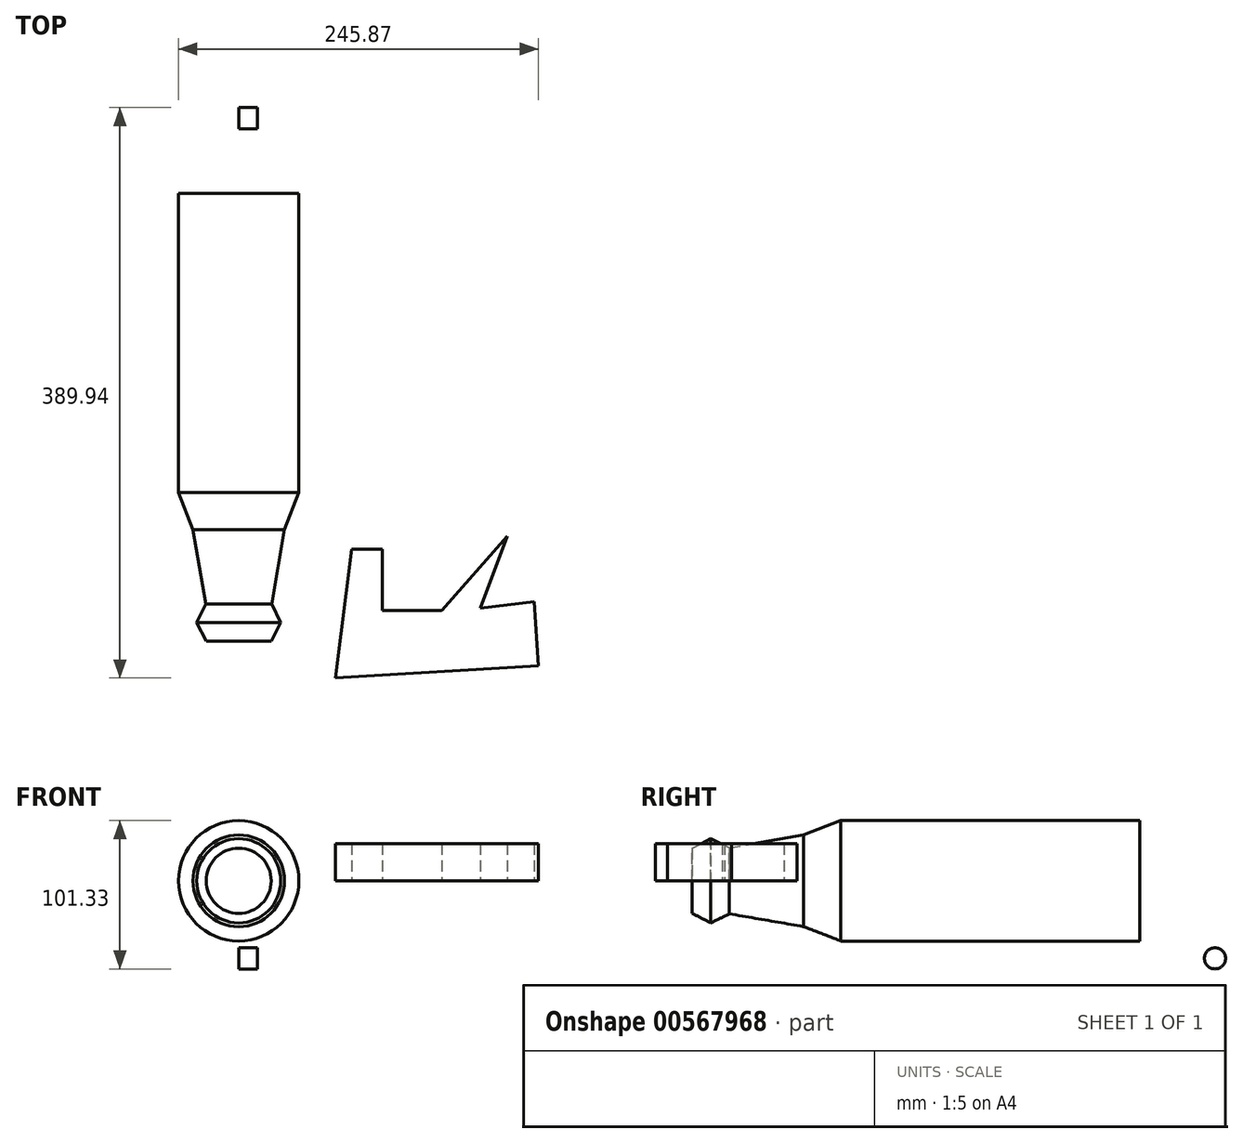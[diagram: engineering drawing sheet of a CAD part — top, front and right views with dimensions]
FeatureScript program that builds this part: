
annotation { "Feature Type Name" : "Feature", "Feature Type Description" : "" }
export const myFeature = defineFeature(function(context is Context, id is Id, definition is map)
    precondition{}
    {
        {
            var Q0;
            Q0=qCreatedBy(makeId("Front.planeOp"),FACE);
            var sketch = newSketch(context, id + "F0", { "sketchPlane" : qUnion([Q0])});
            skCircle(sketch, "E0", {"center": v(0, 0) * mm, "radius": 41.12 * mm});
            skSolve(sketch);
        }
        {
            var Q0;
            Q0 = qSketchRegion(id + "F0", true);
            extrude(context, id + "F1", {"entities" : qUnion([Q0]), "depth" : 204.47 * mm, "offsetDistance" : 25.4 * mm});
        }
        {
            var Q0;
            Q0=makeQuery(id+"F1.opExtrude","CAP_FACE",FACE,{"disambiguationData":[OSD([sQuery(id+"F0.wireOp",EDGE,"E0")])],"isStart":false});
            cPlane(context, id + "F2", {"entities" : qUnion([Q0]), "cplaneType" : CPlaneType.OFFSET, "offset" : 76.2 * mm, "width" : 152.4 * mm, "height" : 152.4 * mm});
        }
        {
            var Q0;
            Q0=makeQuery(id+"F1.opExtrude","CAP_FACE",FACE,{"disambiguationData":[OSD([sQuery(id+"F0.wireOp",EDGE,"E0")])],"isStart":false});
            cPlane(context, id + "F3", {"entities" : qUnion([Q0]), "cplaneType" : CPlaneType.OFFSET, "offset" : 25.4 * mm, "width" : 152.4 * mm, "height" : 152.4 * mm});
        }
        {
            var Q0;
            Q0=qCreatedBy(id+"F3.planeOp",FACE);
            var sketch = newSketch(context, id + "F4", { "sketchPlane" : qUnion([Q0])});
            skCircle(sketch, "E1", {"center": v(0, 0) * mm, "radius": 31.3 * mm});
            skSolve(sketch);
        }
        {
            var Q1;
            Q1=makeQuery(id+"F4.imprint","IMPRINT",FACE,{"disambiguationData":[TD([[makeQuery(id+"F4.imprint","IMPRINT",EDGE,{"derivedFrom":sQuery(id+"F4.wireOp",EDGE,"E1")}),1.0]])]});
            var Q2;
            Q2=makeQuery(id+"F1.opExtrude","CAP_FACE",FACE,{"disambiguationData":[OSD([sQuery(id+"F0.wireOp",EDGE,"E0")])],"isStart":false});
            loft(context, id + "F5", {"operationType" : NewBodyOperationType.ADD, "sheetProfilesArray" : [{ "sheetProfileEntities" : qUnion([Q1]) }, { "sheetProfileEntities" : qUnion([Q2]) }]});
        }
        {
            var Q0;
            Q0=qCreatedBy(id+"F2.planeOp",FACE);
            var sketch = newSketch(context, id + "F6", { "sketchPlane" : qUnion([Q0])});
            skCircle(sketch, "E2", {"center": v(0, 0) * mm, "radius": 22.56 * mm});
            skSolve(sketch);
        }
        {
            var Q1;
            Q1=makeQuery(id+"F5.opLoft","CAP_FACE",FACE,{"disambiguationData":[OSD([makeQuery(id+"F4.imprint","IMPRINT",FACE,{"disambiguationData":[TD([[makeQuery(id+"F4.imprint","IMPRINT",EDGE,{"derivedFrom":sQuery(id+"F4.wireOp",EDGE,"E1")}),1.0]])]})])],"isStart":true});
            var Q2;
            Q2=makeQuery(id+"F6.imprint","IMPRINT",FACE,{"disambiguationData":[TD([[makeQuery(id+"F6.imprint","IMPRINT",EDGE,{"derivedFrom":sQuery(id+"F6.wireOp",EDGE,"E2")}),1.0]])]});
            loft(context, id + "F7", {"operationType" : NewBodyOperationType.ADD, "sheetProfilesArray" : [{ "sheetProfileEntities" : qUnion([Q1]) }, { "sheetProfileEntities" : qUnion([Q2]) }]});
        }
        {
            var Q0;
            Q0=makeQuery(id+"F7.opLoft","CAP_FACE",FACE,{"disambiguationData":[OSD([makeQuery(id+"F6.imprint","IMPRINT",FACE,{"disambiguationData":[TD([[makeQuery(id+"F6.imprint","IMPRINT",EDGE,{"derivedFrom":sQuery(id+"F6.wireOp",EDGE,"E2")}),1.0]])]})])],"isStart":true});
            cPlane(context, id + "F8", {"entities" : qUnion([Q0]), "cplaneType" : CPlaneType.OFFSET, "offset" : 25.4 * mm, "width" : 152.4 * mm, "height" : 152.4 * mm});
        }
        {
            var Q0;
            Q0=qCreatedBy(id+"F2.planeOp",FACE);
            cPlane(context, id + "F9", {"entities" : qUnion([Q0]), "cplaneType" : CPlaneType.OFFSET, "offset" : 12.7 * mm, "width" : 152.4 * mm, "height" : 152.4 * mm});
        }
        {
            var Q0;
            Q0=qCreatedBy(id+"F9.planeOp",FACE);
            var sketch = newSketch(context, id + "F10", { "sketchPlane" : qUnion([Q0])});
            skCircle(sketch, "E3", {"center": v(0, 0) * mm, "radius": 28.76 * mm});
            skSolve(sketch);
        }
        {
            var Q0;
            Q0=qCreatedBy(id+"F8.planeOp",FACE);
            var sketch = newSketch(context, id + "F11", { "sketchPlane" : qUnion([Q0])});
            skCircle(sketch, "E4", {"center": v(0, 0) * mm, "radius": 22.25 * mm});
            skSolve(sketch);
        }
        {
            var Q1;
            Q1=makeQuery(id+"F7.opLoft","CAP_FACE",FACE,{"disambiguationData":[OSD([makeQuery(id+"F6.imprint","IMPRINT",FACE,{"disambiguationData":[TD([[makeQuery(id+"F6.imprint","IMPRINT",EDGE,{"derivedFrom":sQuery(id+"F6.wireOp",EDGE,"E2")}),1.0]])]})])],"isStart":true});
            var Q2;
            Q2=makeQuery(id+"F10.imprint","IMPRINT",FACE,{"disambiguationData":[TD([[makeQuery(id+"F10.imprint","IMPRINT",EDGE,{"derivedFrom":sQuery(id+"F10.wireOp",EDGE,"E3")}),1.0]])]});
            loft(context, id + "F12", {"operationType" : NewBodyOperationType.ADD, "sheetProfilesArray" : [{ "sheetProfileEntities" : qUnion([Q1]) }, { "sheetProfileEntities" : qUnion([Q2]) }]});
        }
        {
            var Q1;
            Q1=makeQuery(id+"F12.opLoft","CAP_FACE",FACE,{"disambiguationData":[OSD([makeQuery(id+"F10.imprint","IMPRINT",FACE,{"disambiguationData":[TD([[makeQuery(id+"F10.imprint","IMPRINT",EDGE,{"derivedFrom":sQuery(id+"F10.wireOp",EDGE,"E3")}),1.0]])]})])],"isStart":true});
            var Q2;
            Q2=makeQuery(id+"F11.imprint","IMPRINT",FACE,{"disambiguationData":[TD([[makeQuery(id+"F11.imprint","IMPRINT",EDGE,{"derivedFrom":sQuery(id+"F11.wireOp",EDGE,"E4")}),1.0]])]});
            loft(context, id + "F13", {"operationType" : NewBodyOperationType.ADD, "sheetProfilesArray" : [{ "sheetProfileEntities" : qUnion([Q1]) }, { "sheetProfileEntities" : qUnion([Q2]) }]});
        }
        {
            var Q0;
            Q0=qCreatedBy(makeId("Top.planeOp"),FACE);
            var sketch = newSketch(context, id + "F14", { "sketchPlane" : qUnion([Q0])});
            skLineSegment(sketch, "E5", {"start": v(165.2, -283.81) * mm, "end": v(183.55, -234.47) * mm});
            skLineSegment(sketch, "E6", {"start": v(183.55, -234.47) * mm, "end": v(138.97, -285.4) * mm});
            skLineSegment(sketch, "E7", {"start": v(138.97, -285.4) * mm, "end": v(98.06, -285.4) * mm});
            skLineSegment(sketch, "E8", {"start": v(98.06, -285.4) * mm, "end": v(98.06, -243.28) * mm});
            skLineSegment(sketch, "E9", {"start": v(98.06, -243.28) * mm, "end": v(77.22, -243.28) * mm});
            skLineSegment(sketch, "E10", {"start": v(77.22, -243.28) * mm, "end": v(66.24, -331.4) * mm});
            skLineSegment(sketch, "E11", {"start": v(66.24, -331.4) * mm, "end": v(204.75, -323.07) * mm});
            skLineSegment(sketch, "E12", {"start": v(204.75, -323.07) * mm, "end": v(202.12, -279.22) * mm});
            skLineSegment(sketch, "E13", {"start": v(202.12, -279.22) * mm, "end": v(165.2, -283.81) * mm});
            skSolve(sketch);
        }
        {
            var Q0;
            Q0 = qSketchRegion(id + "F14", true);
            extrude(context, id + "F15", {"entities" : qUnion([Q0]), "depth" : 25.4 * mm, "offsetDistance" : 25.4 * mm});
        }
        {
            var Q0;
            Q0=qCreatedBy(makeId("Right.planeOp"),FACE);
            var sketch = newSketch(context, id + "F16", { "sketchPlane" : qUnion([Q0])});
            skCircle(sketch, "E14", {"center": v(51.31, -52.99) * mm, "radius": 7.23 * mm});
            skSolve(sketch);
        }
        {
            var Q0;
            Q0 = qSketchRegion(id + "F16", true);
            extrude(context, id + "F17", {"entities" : qUnion([Q0]), "depth" : 12.7 * mm, "offsetDistance" : 25.4 * mm});
        }
    });
